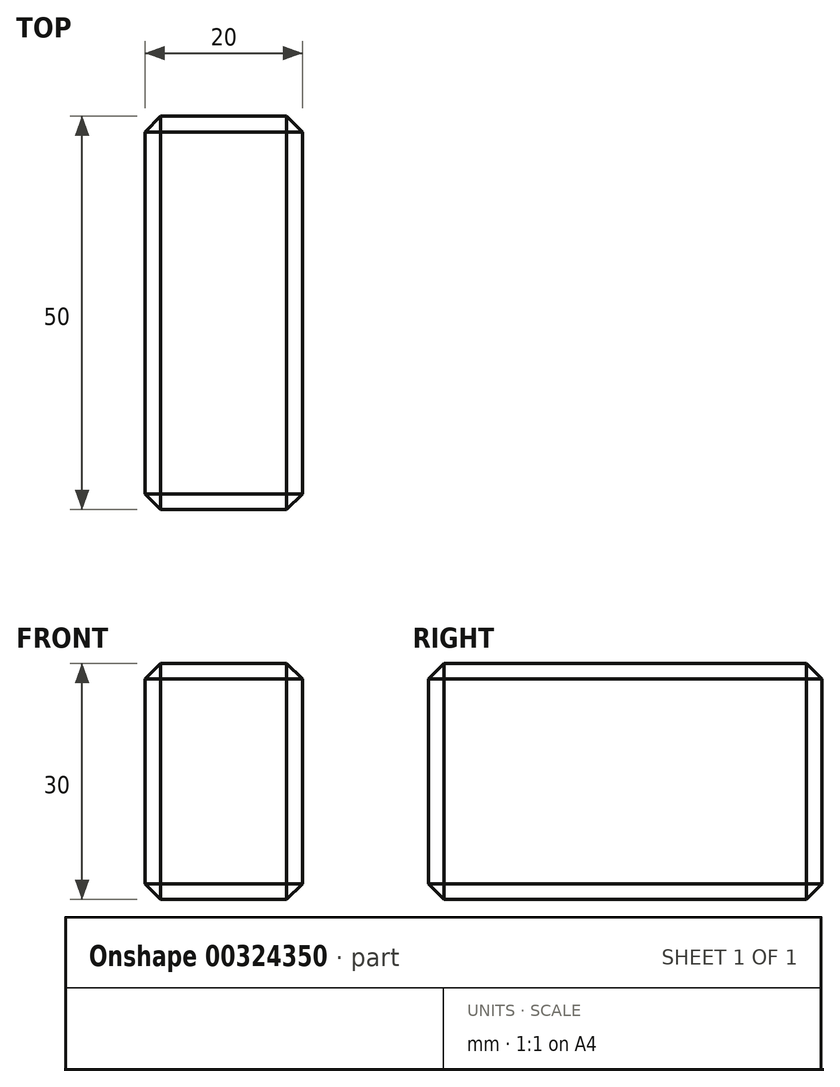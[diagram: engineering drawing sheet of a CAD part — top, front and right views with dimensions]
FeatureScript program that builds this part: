
annotation { "Feature Type Name" : "Feature", "Feature Type Description" : "" }
export const myFeature = defineFeature(function(context is Context, id is Id, definition is map)
    precondition{}
    {
        {
            var Q0;
            Q0=qCreatedBy(makeId("Front.planeOp"),FACE);
            var sketch = newSketch(context, id + "F0", { "sketchPlane" : qUnion([Q0])});
            skLineSegment(sketch, "E0.bottom", {"start": v(10, 15) * mm, "end": v(-10, 15) * mm});
            skLineSegment(sketch, "E0.top", {"start": v(10, -15) * mm, "end": v(-10, -15) * mm});
            skLineSegment(sketch, "E0.left", {"start": v(10, 15) * mm, "end": v(10, -15) * mm});
            skLineSegment(sketch, "E0.right", {"start": v(-10, 15) * mm, "end": v(-10, -15) * mm});
            skPoint(sketch, "E0.middle", {"position": v(0, 0) * mm});
            skSolve(sketch);
        }
        {
            var Q0;
            Q0 = qSketchRegion(id + "F0", true);
            extrude(context, id + "F1", {"entities" : qUnion([Q0]), "depth" : 50 * mm});
        }
        {
            var Q0;
            Q0=makeQuery(id+"F1.opExtrude","CAP_EDGE",EDGE,{"disambiguationData":[OSD([sQuery(id+"F0.wireOp",EDGE,"E0.right")])],"isStart":false});
            var Q1;
            Q1=makeQuery(id+"F1.opExtrude","CAP_EDGE",EDGE,{"disambiguationData":[OSD([sQuery(id+"F0.wireOp",EDGE,"E0.bottom")])],"isStart":false});
            var Q2;
            Q2=makeQuery(id+"F1.opExtrude","CAP_EDGE",EDGE,{"disambiguationData":[OSD([sQuery(id+"F0.wireOp",EDGE,"E0.left")])],"isStart":false});
            var Q3;
            Q3=makeQuery(id+"F1.opExtrude","SWEPT_FACE",FACE,{"disambiguationData":[OSD([sQuery(id+"F0.wireOp",EDGE,"E0.top")])]});
            var Q4;
            Q4=makeQuery(id+"F1.opExtrude","SWEPT_EDGE",EDGE,{"disambiguationData":[OSD([sQuery(id+"F0.wireOp",EDGE,"E0.bottom"),sQuery(id+"F0.wireOp",EDGE,"E0.left")])]});
            var Q5;
            Q5=makeQuery(id+"F1.opExtrude","CAP_EDGE",EDGE,{"disambiguationData":[OSD([sQuery(id+"F0.wireOp",EDGE,"E0.right")])],"isStart":true});
            var Q6;
            Q6=makeQuery(id+"F1.opExtrude","CAP_EDGE",EDGE,{"disambiguationData":[OSD([sQuery(id+"F0.wireOp",EDGE,"E0.left")])],"isStart":true});
            var Q7;
            Q7=makeQuery(id+"F1.opExtrude","CAP_EDGE",EDGE,{"disambiguationData":[OSD([sQuery(id+"F0.wireOp",EDGE,"E0.bottom")])],"isStart":true});
            var Q8;
            Q8=makeQuery(id+"F1.opExtrude","SWEPT_EDGE",EDGE,{"disambiguationData":[OSD([sQuery(id+"F0.wireOp",EDGE,"E0.bottom"),sQuery(id+"F0.wireOp",EDGE,"E0.right")])]});
            chamfer(context, id + "F2", {"entities" : qUnion([Q0, Q1, Q2, Q3, Q4, Q5, Q6, Q7, Q8]), "width" : 2 * mm, "tangentPropagation" : true});
        }
    });
